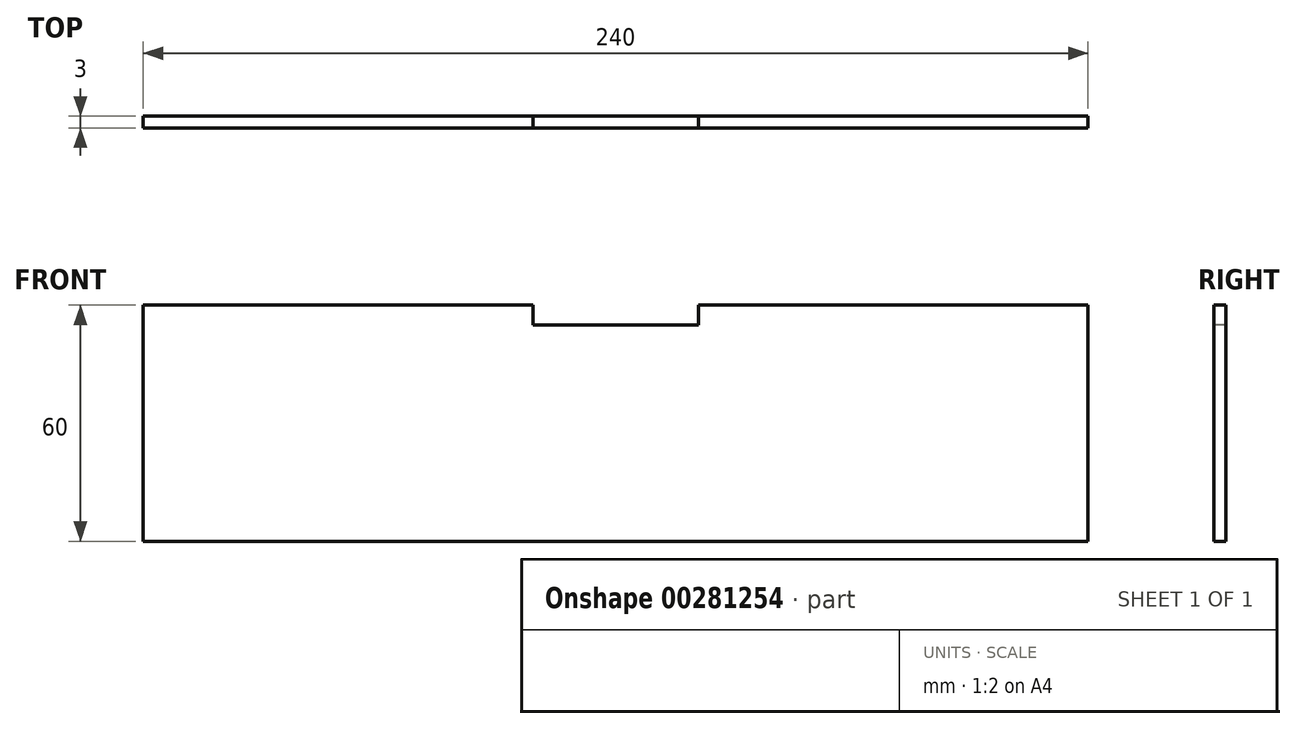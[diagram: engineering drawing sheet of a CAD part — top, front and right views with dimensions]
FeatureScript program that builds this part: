
annotation { "Feature Type Name" : "Feature", "Feature Type Description" : "" }
export const myFeature = defineFeature(function(context is Context, id is Id, definition is map)
    precondition{}
    {
        {
            var Q0;
            Q0=qCreatedBy(makeId("Front.planeOp"),FACE);
            var sketch = newSketch(context, id + "F0", { "sketchPlane" : qUnion([Q0])});
            skLineSegment(sketch, "E0.bottom", {"start": v(120, -30) * mm, "end": v(-120, -30) * mm});
            skLineSegment(sketch, "E0.top", {"start": v(120, 30) * mm, "end": v(-120, 30) * mm});
            skLineSegment(sketch, "E0.left", {"start": v(120, -30) * mm, "end": v(120, 30) * mm});
            skLineSegment(sketch, "E0.right", {"start": v(-120, -30) * mm, "end": v(-120, 30) * mm});
            skPoint(sketch, "E0.middle", {"position": v(0, 0) * mm});
            skSolve(sketch);
        }
        {
            var Q0;
            Q0=qSketchRegion(id+"F0",true);
            extrude(context, id + "F1", {"entities" : qUnion([Q0]), "depth" : 3 * mm});
        }
        {
            var Q0;
            Q0=makeQuery(id+"F1.opExtrude","CAP_FACE",FACE,{"disambiguationData":[OSD([sQuery(id+"F0.wireOp",EDGE,"E0.bottom"),sQuery(id+"F0.wireOp",EDGE,"E0.top"),sQuery(id+"F0.wireOp",EDGE,"E0.left"),sQuery(id+"F0.wireOp",EDGE,"E0.right")])],"isStart":false});
            var sketch = newSketch(context, id + "F2", { "sketchPlane" : qUnion([Q0])});
            skLineSegment(sketch, "E1.bottom", {"start": v(21, 25) * mm, "end": v(-21, 25) * mm});
            skLineSegment(sketch, "E1.top", {"start": v(21, 35) * mm, "end": v(-21, 35) * mm});
            skLineSegment(sketch, "E1.left", {"start": v(21, 25) * mm, "end": v(21, 35) * mm});
            skLineSegment(sketch, "E1.right", {"start": v(-21, 25) * mm, "end": v(-21, 35) * mm});
            skPoint(sketch, "E1.middle", {"position": v(0, 30) * mm});
            skSolve(sketch);
        }
        {
            var Q0;
            Q0=qSketchRegion(id+"F2",true);
            extrude(context, id + "F3", {"entities" : qUnion([Q0]), "operationType" : NewBodyOperationType.REMOVE, "oppositeDirection" : true, "depth" : 25 * mm});
        }
    });
